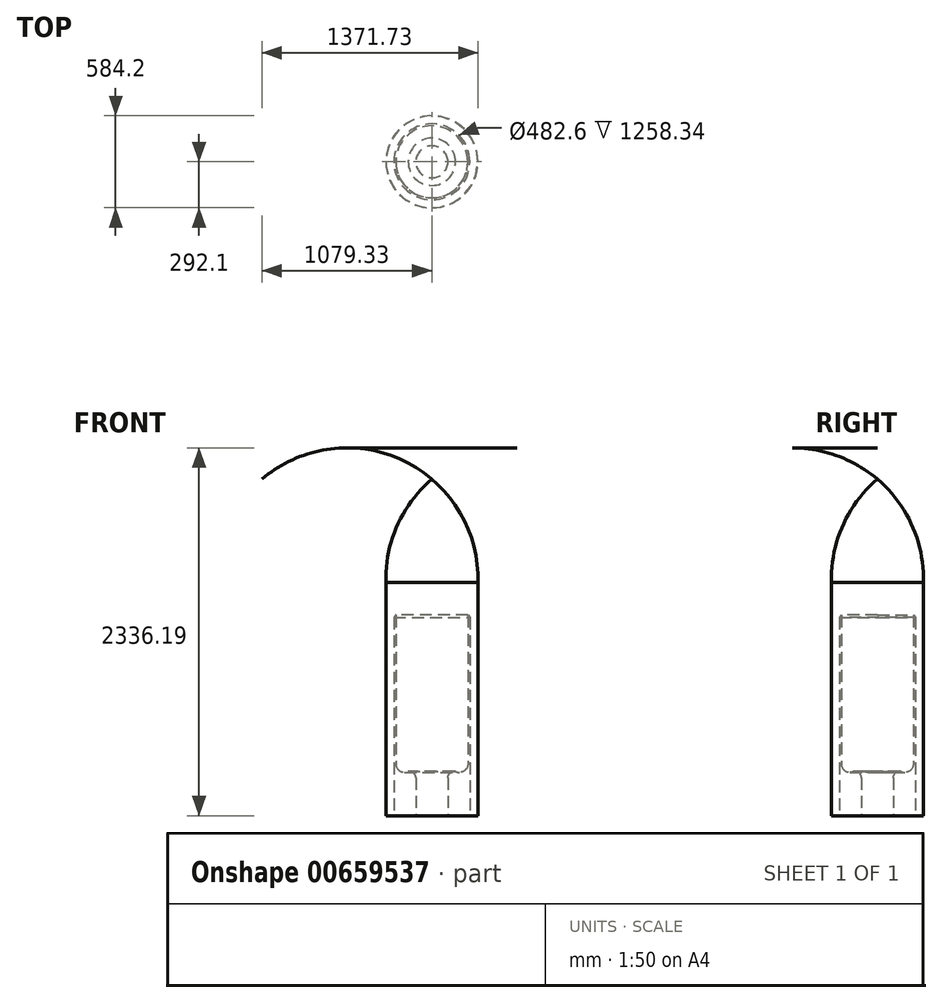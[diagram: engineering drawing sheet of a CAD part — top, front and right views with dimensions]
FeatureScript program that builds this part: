
annotation { "Feature Type Name" : "Feature", "Feature Type Description" : "" }
export const myFeature = defineFeature(function(context is Context, id is Id, definition is map)
    precondition{}
    {
        {
            var Q0;
            Q0=qCreatedBy(makeId("Right.planeOp"),FACE);
            var sketch = newSketch(context, id + "F0", { "sketchPlane" : qUnion([Q0])});
            skLineSegment(sketch, "E0", {"start": v(0, 0) * mm, "end": v(0, 1625.6) * mm});
            skLineSegment(sketch, "E1", {"start": v(228.6, 1269.54) * mm, "end": v(228.6, 329.6) * mm});
            skLineSegment(sketch, "E2", {"start": v(0, 0) * mm, "end": v(101.6, 0) * mm});
            skLineSegment(sketch, "E3", {"start": v(101.6, 0) * mm, "end": v(101.6, 240.02) * mm});
            skArc(sketch, "E4", {"start": v(228.6, 1269.54) * mm, "mid": v(166.53, 1481.1) * mm, "end": v(0, 1625.6) * mm});
            skArc(sketch, "E5", {"start": v(150.14, 280.86) * mm, "mid": v(202.92, 283.42) * mm, "end": v(228.6, 329.6) * mm});
            skArc(sketch, "E6", {"start": v(150.14, 280.86) * mm, "mid": v(116.36, 271.73) * mm, "end": v(101.6, 240.02) * mm});
            skSolve(sketch);
        }
        {
            var Q0;
            Q0=makeQuery(id+"F0.imprint","IMPRINT",FACE,{"disambiguationData":[TD([[makeQuery(id+"F0.imprint","IMPRINT",EDGE,{"derivedFrom":sQuery(id+"F0.wireOp",EDGE,"E0")}),-1.0]])]});
            var Q1;
            Q1=sQuery(id+"F0.wireOp",EDGE,"E0");
            revolve(context, id + "F1", {"entities" : qUnion([Q0]), "axis" : qUnion([Q1]), "revolveType" : RevolveType.FULL});
        }
        {
            var Q0;
            Q0=qCreatedBy(makeId("Right.planeOp"),FACE);
            var sketch = newSketch(context, id + "F2", { "sketchPlane" : qUnion([Q0])});
            skLineSegment(sketch, "E7", {"start": v(0, 0) * mm, "end": v(0, 2137.44) * mm});
            skArc(sketch, "E8", {"start": v(292.1, 1481.6) * mm, "mid": v(220.42, 1842.65) * mm, "end": v(0, 2137.44) * mm});
            skLineSegment(sketch, "E9", {"start": v(292.1, 1481.6) * mm, "end": v(292.1, 0) * mm});
            skLineSegment(sketch, "E10", {"start": v(0, 1588.59) * mm, "end": v(241.3, 1258.34) * mm});
            skLineSegment(sketch, "E11", {"start": v(241.3, 1258.34) * mm, "end": v(241.3, 0) * mm});
            skLineSegment(sketch, "E12", {"start": v(292.1, 0) * mm, "end": v(241.3, 0) * mm});
            skSolve(sketch);
        }
        {
            var Q0;
            {var subQ1=sQuery(id+"F2.wireOp",EDGE,"E8");Q0=makeQuery(id+"F2.imprint","IMPRINT",FACE,{"disambiguationData":[TD([[makeQuery(id+"F2.imprint","IMPRINT",EDGE,{"derivedFrom":subQ1}),1.0]])]});}
            var Q1;
            Q1=sQuery(id+"F2.wireOp",EDGE,"E7");
            revolve(context, id + "F3", {"operationType" : NewBodyOperationType.ADD, "entities" : qUnion([Q0]), "axis" : qUnion([Q1]), "revolveType" : RevolveType.FULL});
        }
    });
